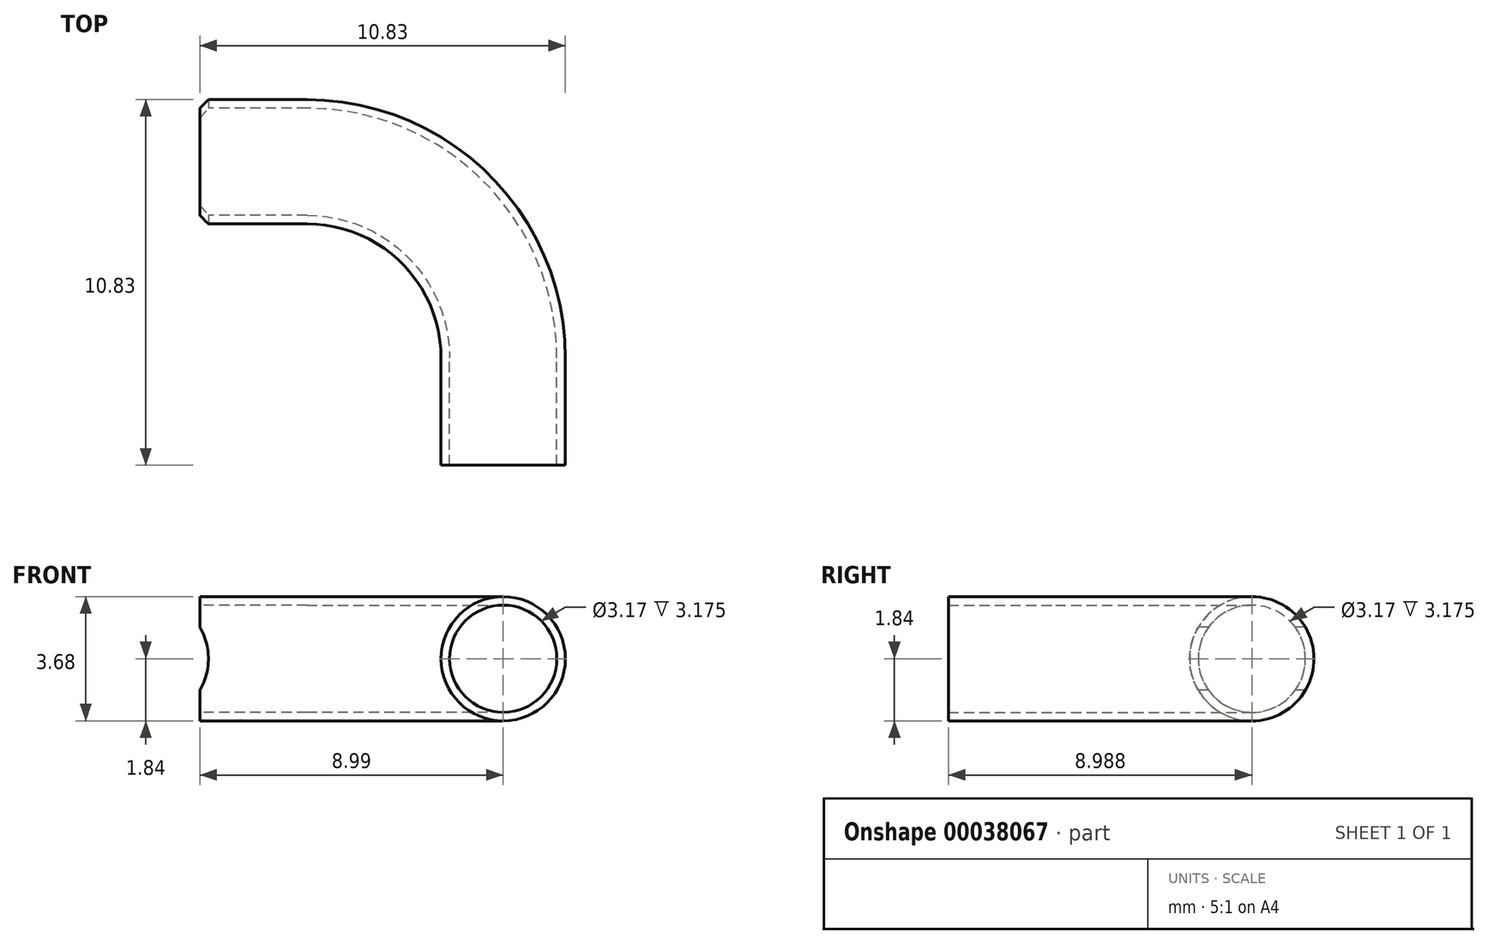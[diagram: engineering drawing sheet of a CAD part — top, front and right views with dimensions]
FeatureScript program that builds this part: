
annotation { "Feature Type Name" : "Feature", "Feature Type Description" : "" }
export const myFeature = defineFeature(function(context is Context, id is Id, definition is map)
    precondition{}
    {
        {
            var Q0;
            Q0=qCreatedBy(makeId("Top.planeOp"),FACE);
            var sketch = newSketch(context, id + "F0", { "sketchPlane" : qUnion([Q0])});
            skLineSegment(sketch, "E0", {"start": v(0, 0) * mm, "end": v(0, 3.18) * mm});
            skArc(sketch, "E1", {"start": v(0, 3.18) * mm, "mid": v(-1.7, 7.29) * mm, "end": v(-5.81, 8.99) * mm});
            skLineSegment(sketch, "E2", {"start": v(0, 0) * mm, "end": v(-8.99, 0) * mm, "construction": true});
            skLineSegment(sketch, "E3", {"start": v(-8.99, 0) * mm, "end": v(-8.99, 8.99) * mm, "construction": true});
            skLineSegment(sketch, "E4", {"start": v(-8.99, 8.99) * mm, "end": v(-5.81, 8.99) * mm});
            skSolve(sketch);
        }
        {
            var Q0;
            Q0=qCreatedBy(makeId("Front.planeOp"),FACE);
            var sketch = newSketch(context, id + "F1", { "sketchPlane" : qUnion([Q0])});
            skCircle(sketch, "E5", {"center": v(0, 0) * mm, "radius": 1.84 * mm, "construction": true});
            skCircle(sketch, "E6", {"center": v(0, 0) * mm, "radius": 1.59 * mm});
            skLineSegment(sketch, "E7.rect.bottom", {"start": v(1.84, 1.84) * mm, "end": v(-1.84, 1.84) * mm});
            skLineSegment(sketch, "E7.rect.top", {"start": v(1.84, -1.84) * mm, "end": v(-1.84, -1.84) * mm});
            skLineSegment(sketch, "E7.rect.left", {"start": v(1.84, 1.84) * mm, "end": v(1.84, -1.84) * mm});
            skLineSegment(sketch, "E7.rect.right", {"start": v(-1.84, 1.84) * mm, "end": v(-1.84, -1.84) * mm});
            skSolve(sketch);
        }
        {
            var Q0;
            Q0=makeQuery(id+"F1.imprint","IMPRINT",FACE,{"disambiguationData":[TD([[makeQuery(id+"F1.imprint","IMPRINT",EDGE,{"derivedFrom":sQuery(id+"F1.wireOp",EDGE,"E6")}),-1.0]])]});
            var Q1;
            Q1=sQuery(id+"F0.wireOp",EDGE,"E1");
            var Q2;
            Q2=sQuery(id+"F0.wireOp",EDGE,"E4");
            var Q3;
            Q3=sQuery(id+"F0.wireOp",EDGE,"E0");
            sweep(context, id + "F2", {"profiles" : qUnion([Q0]), "path" : qUnion([Q1, Q2, Q3])});
        }
        {
            var Q0;
            Q0=makeQuery(id+"F2.opSweep","SWEPT_FACE",FACE,{"disambiguationData":[OSD([sQuery(id+"F0.wireOp",EDGE,"E4"),sQuery(id+"F1.wireOp",EDGE,"E7.rect.right")])]});
            var sketch = newSketch(context, id + "F3", { "sketchPlane" : qUnion([Q0])});
            skArc(sketch, "E8", {"start": v(-8.99, -0.93) * mm, "mid": v(-8.73, 0) * mm, "end": v(-8.99, 0.93) * mm});
            skLineSegment(sketch, "E9", {"start": v(-8.99, 0) * mm, "end": v(-10.57, 0) * mm});
            skLineSegment(sketch, "E10", {"start": v(-8.99, 0.93) * mm, "end": v(-8.99, -0.93) * mm});
            skSolve(sketch);
        }
        {
            var Q0;
            Q0 = qSketchRegion(id + "F3", true);
            var Q1;
            Q1=makeQuery(id+"F2.opSweep","SWEPT_FACE",FACE,{"disambiguationData":[OSD([sQuery(id+"F0.wireOp",EDGE,"E4"),sQuery(id+"F1.wireOp",EDGE,"E7.rect.left")])]});
            extrude(context, id + "F4", {"entities" : qUnion([Q0]), "operationType" : NewBodyOperationType.REMOVE, "endBound" : BoundingType.UP_TO_SURFACE, "oppositeDirection" : true, "endBoundEntityFace" : qUnion([Q1]), "depth" : 25.4 * mm});
        }
        {
            var Q0;
            Q0=makeQuery(id+"F2.opSweep","SWEPT_EDGE",EDGE,{"disambiguationData":[OSD([sQuery(id+"F0.wireOp",EDGE,"E1"),sQuery(id+"F1.wireOp",EDGE,"E7.rect.bottom"),sQuery(id+"F1.wireOp",EDGE,"E7.rect.right")])]});
            var Q1;
            Q1=makeQuery(id+"F2.opSweep","SWEPT_EDGE",EDGE,{"disambiguationData":[OSD([sQuery(id+"F0.wireOp",EDGE,"E1"),sQuery(id+"F1.wireOp",EDGE,"E7.rect.top"),sQuery(id+"F1.wireOp",EDGE,"E7.rect.right")])]});
            var Q2;
            Q2=makeQuery(id+"F2.opSweep","SWEPT_EDGE",EDGE,{"disambiguationData":[OSD([sQuery(id+"F0.wireOp",EDGE,"E1"),sQuery(id+"F1.wireOp",EDGE,"E7.rect.bottom"),sQuery(id+"F1.wireOp",EDGE,"E7.rect.left")])]});
            var Q3;
            Q3=makeQuery(id+"F2.opSweep","SWEPT_EDGE",EDGE,{"disambiguationData":[OSD([sQuery(id+"F0.wireOp",EDGE,"E1"),sQuery(id+"F1.wireOp",EDGE,"E7.rect.top"),sQuery(id+"F1.wireOp",EDGE,"E7.rect.left")])]});
            fillet(context, id + "F5", {"entities" : qUnion([Q0, Q1, Q2, Q3]), "radius" : 1.84 * mm, "tangentPropagation" : true, "allowEdgeOverflow" : false});
        }
    });
